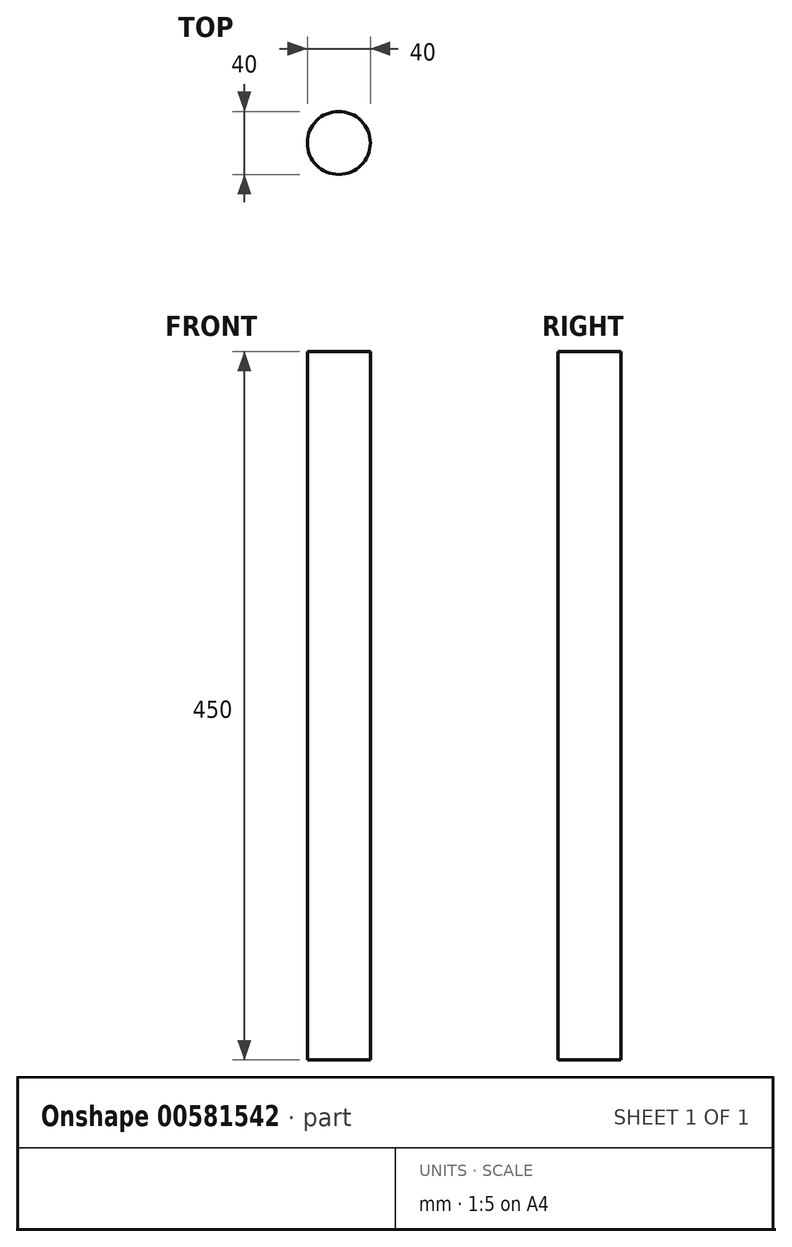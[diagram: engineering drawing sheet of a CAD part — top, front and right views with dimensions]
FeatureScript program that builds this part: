
annotation { "Feature Type Name" : "Feature", "Feature Type Description" : "" }
export const myFeature = defineFeature(function(context is Context, id is Id, definition is map)
    precondition{}
    {
        {
            var Q0;
            Q0=qCreatedBy(makeId("Top.planeOp"),FACE);
            var sketch = newSketch(context, id + "F0", { "sketchPlane" : qUnion([Q0])});
            skCircle(sketch, "E0", {"center": v(-9.84, 9.55) * mm, "radius": 20 * mm});
            skSolve(sketch);
        }
        {
            var Q0;
            Q0=makeQuery(id+"F0.imprint","IMPRINT",FACE,{"disambiguationData":[TD([[makeQuery(id+"F0.imprint","IMPRINT",EDGE,{"derivedFrom":sQuery(id+"F0.wireOp",EDGE,"E0")}),1.0]])]});
            extrude(context, id + "F1", {"entities" : qUnion([Q0]), "depth" : 450 * mm, "offsetDistance" : 25 * mm});
        }
    });
